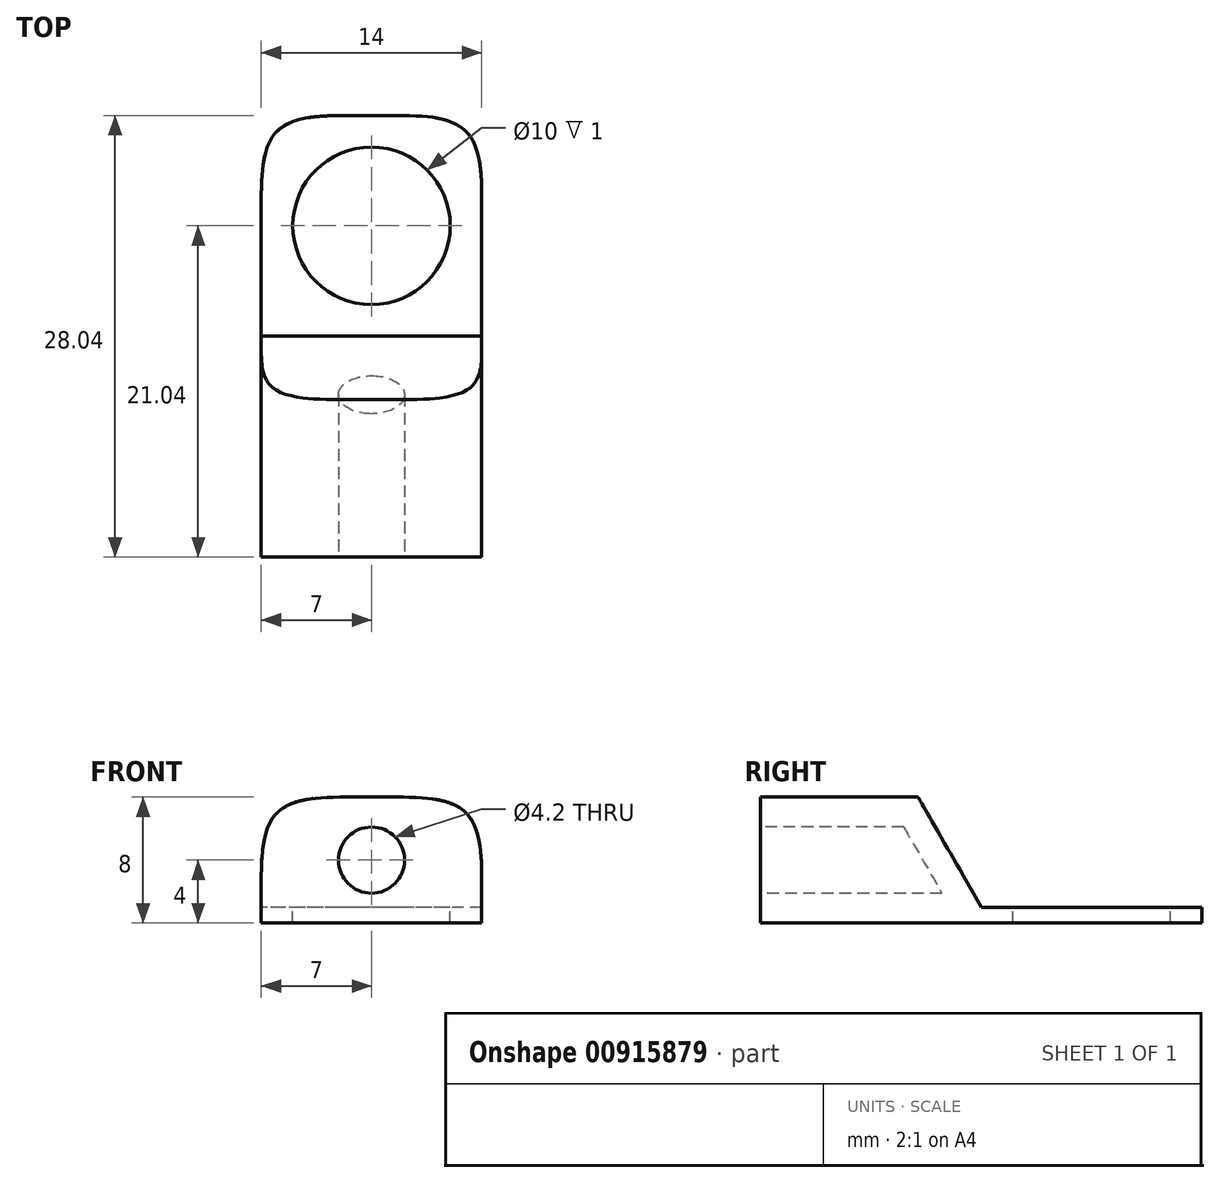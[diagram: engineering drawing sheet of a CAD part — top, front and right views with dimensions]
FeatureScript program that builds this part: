
annotation { "Feature Type Name" : "Feature", "Feature Type Description" : "" }
export const myFeature = defineFeature(function(context is Context, id is Id, definition is map)
    precondition{}
    {
        {
            var Q0;
            Q0=qCreatedBy(makeId("Right.planeOp"),FACE);
            var sketch = newSketch(context, id + "F0", { "sketchPlane" : qUnion([Q0])});
            skLineSegment(sketch, "E0", {"start": v(-21.04, 0) * mm, "end": v(7, 0) * mm});
            skLineSegment(sketch, "E1", {"start": v(7, 0) * mm, "end": v(7, 1) * mm});
            skLineSegment(sketch, "E2", {"start": v(7, 1) * mm, "end": v(-7, 1) * mm});
            skLineSegment(sketch, "E3", {"start": v(-7, 1) * mm, "end": v(-11.04, 8) * mm});
            skLineSegment(sketch, "E4", {"start": v(-11.04, 8) * mm, "end": v(-21.04, 8) * mm});
            skLineSegment(sketch, "E5", {"start": v(-21.04, 8) * mm, "end": v(-21.04, 0) * mm});
            skSolve(sketch);
        }
        {
            var Q0;
            Q0 = qSketchRegion(id + "F0", true);
            extrude(context, id + "F1", {"entities" : qUnion([Q0]), "endBound" : BoundingType.SYMMETRIC, "depth" : 14 * mm, "offsetDistance" : 25 * mm});
        }
        {
            var Q0;
            Q0=makeQuery(id+"F1.opExtrude","SWEPT_FACE",FACE,{"disambiguationData":[OSD([sQuery(id+"F0.wireOp",EDGE,"E5")])]});
            var sketch = newSketch(context, id + "F2", { "sketchPlane" : qUnion([Q0])});
            skCircle(sketch, "E6", {"center": v(0, 4) * mm, "radius": 2.1 * mm});
            skLineSegment(sketch, "E7", {"start": v(0, 0) * mm, "end": v(0, 8) * mm, "construction": true});
            skSolve(sketch);
        }
        {
            var Q0;
            Q0 = qSketchRegion(id + "F2", true);
            var Q1;
            Q1=makeQuery(id+"F1.opExtrude","SWEPT_FACE",FACE,{"disambiguationData":[OSD([sQuery(id+"F0.wireOp",EDGE,"E3")])]});
            extrude(context, id + "F3", {"entities" : qUnion([Q0]), "operationType" : NewBodyOperationType.REMOVE, "endBound" : BoundingType.UP_TO_SURFACE, "oppositeDirection" : true, "depth" : 4 * mm, "endBoundEntityFace" : qUnion([Q1]), "hasOffset" : true, "offsetDistance" : 2 * mm});
        }
        {
            var Q0;
            Q0=makeQuery(id+"F1.opExtrude","CAP_EDGE",EDGE,{"disambiguationData":[OSD([sQuery(id+"F0.wireOp",EDGE,"E1")])],"isStart":false});
            var Q1;
            Q1=makeQuery(id+"F1.opExtrude","CAP_EDGE",EDGE,{"disambiguationData":[OSD([sQuery(id+"F0.wireOp",EDGE,"E1")])],"isStart":true});
            var Q2;
            Q2=makeQuery(id+"F1.opExtrude","CAP_EDGE",EDGE,{"disambiguationData":[OSD([sQuery(id+"F0.wireOp",EDGE,"E4")])],"isStart":true});
            var Q3;
            Q3=makeQuery(id+"F1.opExtrude","CAP_EDGE",EDGE,{"disambiguationData":[OSD([sQuery(id+"F0.wireOp",EDGE,"E4")])],"isStart":false});
            fillet(context, id + "F4", {"entities" : qUnion([Q0, Q1, Q2, Q3]), "radius" : 5 * mm, "tangentPropagation" : true, "rho" : .6, "crossSection" : FilletCrossSection.CONIC, "allowEdgeOverflow" : false});
        }
        {
            var Q0;
            Q0=makeQuery(id+"F1.opExtrude","SWEPT_FACE",FACE,{"disambiguationData":[OSD([sQuery(id+"F0.wireOp",EDGE,"E2")])]});
            var sketch = newSketch(context, id + "F5", { "sketchPlane" : qUnion([Q0])});
            skCircle(sketch, "E8", {"center": v(0, 0) * mm, "radius": 5 * mm});
            skSolve(sketch);
        }
        {
            var Q0;
            Q0 = qSketchRegion(id + "F5", true);
            extrude(context, id + "F6", {"entities" : qUnion([Q0]), "operationType" : NewBodyOperationType.REMOVE, "endBound" : BoundingType.UP_TO_NEXT, "oppositeDirection" : true, "depth" : 25 * mm, "offsetDistance" : 25 * mm});
        }
    });
